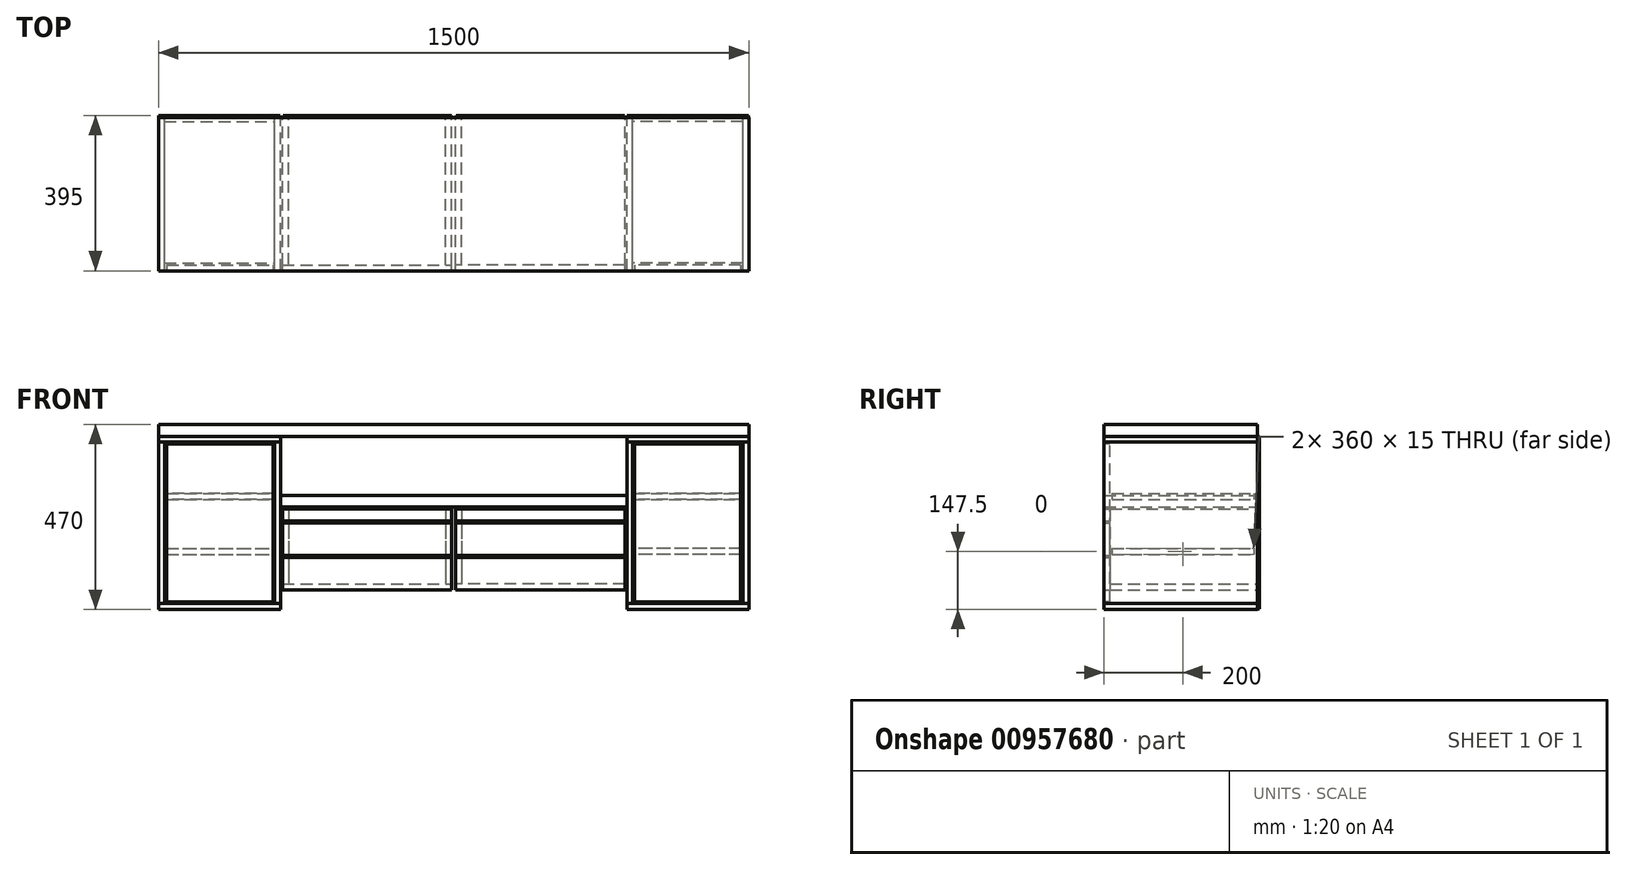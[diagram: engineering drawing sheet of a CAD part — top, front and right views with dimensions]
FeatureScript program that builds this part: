
annotation { "Feature Type Name" : "Feature", "Feature Type Description" : "" }
export const myFeature = defineFeature(function(context is Context, id is Id, definition is map)
    precondition{}
    {
        {
            var Q0;
            Q0=qCreatedBy(makeId("Top.planeOp"),FACE);
            var sketch = newSketch(context, id + "F0", { "sketchPlane" : qUnion([Q0])});
            skLineSegment(sketch, "E0.bottom", {"start": v(0, 0) * mm, "end": v(310, 0) * mm});
            skLineSegment(sketch, "E0.top", {"start": v(0, 390) * mm, "end": v(310, 390) * mm});
            skLineSegment(sketch, "E0.left", {"start": v(0, 0) * mm, "end": v(0, 390) * mm});
            skLineSegment(sketch, "E0.right", {"start": v(310, 0) * mm, "end": v(310, 390) * mm});
            skSolve(sketch);
        }
        {
            var Q0;
            Q0 = qSketchRegion(id + "F0", true);
            extrude(context, id + "F1", {"entities" : qUnion([Q0]), "depth" : 15 * mm, "offsetDistance" : 25 * mm});
        }
        {
            var Q0;
            Q0=makeQuery(id+"F1.opExtrude","CAP_FACE",FACE,{"disambiguationData":[OSD([sQuery(id+"F0.wireOp",EDGE,"E0.bottom"),sQuery(id+"F0.wireOp",EDGE,"E0.top"),sQuery(id+"F0.wireOp",EDGE,"E0.left"),sQuery(id+"F0.wireOp",EDGE,"E0.right")])],"isStart":false});
            cPlane(context, id + "F2", {"entities" : qUnion([Q0]), "cplaneType" : CPlaneType.OFFSET, "offset" : 0 * mm, "width" : 150 * mm, "height" : 150 * mm});
        }
        {
            var Q0;
            Q0=qCreatedBy(id+"F2.planeOp",FACE);
            var sketch = newSketch(context, id + "F3", { "sketchPlane" : qUnion([Q0])});
            skLineSegment(sketch, "E1.bottom", {"start": v(0, 0) * mm, "end": v(15, 0) * mm});
            skLineSegment(sketch, "E1.top", {"start": v(0, 390) * mm, "end": v(15, 390) * mm});
            skLineSegment(sketch, "E1.left", {"start": v(0, 0) * mm, "end": v(0, 390) * mm});
            skLineSegment(sketch, "E1.right", {"start": v(15, 0) * mm, "end": v(15, 390) * mm});
            skLineSegment(sketch, "E2.bottom", {"start": v(310, 0) * mm, "end": v(295, 0) * mm});
            skLineSegment(sketch, "E2.top", {"start": v(310, 390) * mm, "end": v(295, 390) * mm});
            skLineSegment(sketch, "E2.left", {"start": v(310, 0) * mm, "end": v(310, 390) * mm});
            skLineSegment(sketch, "E2.right", {"start": v(295, 0) * mm, "end": v(295, 390) * mm});
            skSolve(sketch);
        }
        {
            var Q0;
            Q0 = qSketchRegion(id + "F3", true);
            extrude(context, id + "F4", {"entities" : qUnion([Q0]), "depth" : 410 * mm, "offsetDistance" : 25 * mm});
        }
        {
            var Q0;
            Q0=makeQuery(id+"F4.opExtrude","CAP_FACE",FACE,{"disambiguationData":[OSD([sQuery(id+"F3.wireOp",EDGE,"E1.bottom"),sQuery(id+"F3.wireOp",EDGE,"E1.top"),sQuery(id+"F3.wireOp",EDGE,"E1.left"),sQuery(id+"F3.wireOp",EDGE,"E1.right")])],"isStart":false});
            var sketch = newSketch(context, id + "F5", { "sketchPlane" : qUnion([Q0])});
            skLineSegment(sketch, "E3.bottom", {"start": v(0, 0) * mm, "end": v(310, 0) * mm});
            skLineSegment(sketch, "E3.top", {"start": v(0, 390) * mm, "end": v(310, 390) * mm});
            skLineSegment(sketch, "E3.left", {"start": v(0, 0) * mm, "end": v(0, 390) * mm});
            skLineSegment(sketch, "E3.right", {"start": v(310, 0) * mm, "end": v(310, 390) * mm});
            skSolve(sketch);
        }
        {
            var Q0;
            Q0 = qSketchRegion(id + "F5", true);
            extrude(context, id + "F6", {"entities" : qUnion([Q0]), "depth" : 15 * mm, "offsetDistance" : 25 * mm});
        }
        {
            var Q0;
            Q0=makeQuery(id+"F6.opExtrude","SWEPT_FACE",FACE,{"disambiguationData":[OSD([sQuery(id+"F5.wireOp",EDGE,"E3.top")])]});
            var sketch = newSketch(context, id + "F7", { "sketchPlane" : qUnion([Q0])});
            skLineSegment(sketch, "E4.bottom", {"start": v(-1, 1) * mm, "end": v(-309, 1) * mm});
            skLineSegment(sketch, "E4.top", {"start": v(-1, 439) * mm, "end": v(-309, 439) * mm});
            skLineSegment(sketch, "E4.left", {"start": v(-1, 1) * mm, "end": v(-1, 439) * mm});
            skLineSegment(sketch, "E4.right", {"start": v(-309, 1) * mm, "end": v(-309, 439) * mm});
            skPoint(sketch, "E5", {"position": v(-310, 432.5) * mm});
            skSolve(sketch);
        }
        {
            var Q0;
            Q0 = qSketchRegion(id + "F7", true);
            extrude(context, id + "F8", {"entities" : qUnion([Q0]), "depth" : 5 * mm, "offsetDistance" : 25 * mm});
        }
        {
            var Q0;
            Q0=makeQuery(id+"F1.opExtrude","CAP_FACE",FACE,{"disambiguationData":[OSD([sQuery(id+"F0.wireOp",EDGE,"E0.bottom"),sQuery(id+"F0.wireOp",EDGE,"E0.top"),sQuery(id+"F0.wireOp",EDGE,"E0.left"),sQuery(id+"F0.wireOp",EDGE,"E0.right")])],"isStart":false});
            cPlane(context, id + "F9", {"entities" : qUnion([Q0]), "cplaneType" : CPlaneType.OFFSET, "offset" : 125 * mm, "width" : 150 * mm, "height" : 150 * mm});
        }
        {
            var Q0;
            Q0=makeQuery(id+"F1.opExtrude","CAP_FACE",FACE,{"disambiguationData":[OSD([sQuery(id+"F0.wireOp",EDGE,"E0.bottom"),sQuery(id+"F0.wireOp",EDGE,"E0.top"),sQuery(id+"F0.wireOp",EDGE,"E0.left"),sQuery(id+"F0.wireOp",EDGE,"E0.right")])],"isStart":false});
            cPlane(context, id + "F10", {"entities" : qUnion([Q0]), "cplaneType" : CPlaneType.OFFSET, "offset" : (125 + 125 + 15) * mm, "width" : 150 * mm, "height" : 150 * mm});
        }
        {
            var Q0;
            Q0=qCreatedBy(id+"F9.planeOp",FACE);
            var sketch = newSketch(context, id + "F11", { "sketchPlane" : qUnion([Q0])});
            skLineSegment(sketch, "E6.bottom", {"start": v(15, 20) * mm, "end": v(295, 20) * mm});
            skLineSegment(sketch, "E6.top", {"start": v(15, 380) * mm, "end": v(295, 380) * mm});
            skLineSegment(sketch, "E6.left", {"start": v(15, 20) * mm, "end": v(15, 380) * mm});
            skLineSegment(sketch, "E6.right", {"start": v(295, 20) * mm, "end": v(295, 380) * mm});
            skSolve(sketch);
        }
        {
            var Q0;
            Q0 = qSketchRegion(id + "F11", true);
            extrude(context, id + "F12", {"entities" : qUnion([Q0]), "operationType" : NewBodyOperationType.ADD, "depth" : 15 * mm, "offsetDistance" : 25 * mm});
        }
        {
            var Q0;
            Q0=qCreatedBy(id+"F10.planeOp",FACE);
            var sketch = newSketch(context, id + "F13", { "sketchPlane" : qUnion([Q0])});
            skLineSegment(sketch, "E7.0.0", {"start": v(295, 380) * mm, "end": v(15, 380) * mm});
            skLineSegment(sketch, "E7.0.1", {"start": v(15, 380) * mm, "end": v(15, 20) * mm});
            skLineSegment(sketch, "E7.0.2", {"start": v(15, 20) * mm, "end": v(295, 20) * mm});
            skLineSegment(sketch, "E7.0.3", {"start": v(295, 20) * mm, "end": v(295, 380) * mm});
            skSolve(sketch);
        }
        {
            var Q0;
            Q0 = qSketchRegion(id + "F13", true);
            extrude(context, id + "F14", {"entities" : qUnion([Q0]), "depth" : 15 * mm, "offsetDistance" : 25 * mm});
        }
        {
            var Q0;
            Q0=makeQuery(id+"F4.opExtrude","SWEPT_FACE",FACE,{"disambiguationData":[OSD([sQuery(id+"F3.wireOp",EDGE,"E2.bottom")])]});
            var sketch = newSketch(context, id + "F15", { "sketchPlane" : qUnion([Q0])});
            skLineSegment(sketch, "E8.bottom", {"start": v(21, 19) * mm, "end": v(291, 19) * mm});
            skLineSegment(sketch, "E8.top", {"start": v(21, 421) * mm, "end": v(291, 421) * mm});
            skLineSegment(sketch, "E8.left", {"start": v(21, 19) * mm, "end": v(21, 421) * mm});
            skLineSegment(sketch, "E8.right", {"start": v(291, 19) * mm, "end": v(291, 421) * mm});
            skSolve(sketch);
        }
        {
            var Q0;
            Q0 = qSketchRegion(id + "F15", true);
            extrude(context, id + "F16", {"entities" : qUnion([Q0]), "oppositeDirection" : true, "depth" : 15 * mm, "offsetDistance" : 25 * mm});
        }
        {
            var Q0;
            Q0=qCreatedBy(makeId("Right.planeOp"),FACE);
            cPlane(context, id + "F17", {"entities" : qUnion([Q0]), "cplaneType" : CPlaneType.OFFSET, "offset" : 750 * mm, "width" : 150 * mm, "height" : 150 * mm});
        }
        {
            var Q0;
            Q0=makeQuery(id+"F1.opExtrude","SWEPT_BODY",BODY,{"disambiguationData":[OSD([sQuery(id+"F0.wireOp",EDGE,"E0.bottom"),sQuery(id+"F0.wireOp",EDGE,"E0.top"),sQuery(id+"F0.wireOp",EDGE,"E0.left"),sQuery(id+"F0.wireOp",EDGE,"E0.right")])]});
            var Q1;
            Q1=makeQuery(id+"F4.opExtrude","SWEPT_BODY",BODY,{"disambiguationData":[OSD([sQuery(id+"F3.wireOp",EDGE,"E1.bottom"),sQuery(id+"F3.wireOp",EDGE,"E1.top"),sQuery(id+"F3.wireOp",EDGE,"E1.left"),sQuery(id+"F3.wireOp",EDGE,"E1.right")])]});
            var Q2;
            Q2=makeQuery(id+"F4.opExtrude","SWEPT_BODY",BODY,{"disambiguationData":[OSD([sQuery(id+"F3.wireOp",EDGE,"E2.bottom"),sQuery(id+"F3.wireOp",EDGE,"E2.top"),sQuery(id+"F3.wireOp",EDGE,"E2.left"),sQuery(id+"F3.wireOp",EDGE,"E2.right")])]});
            var Q3;
            Q3=makeQuery(id+"F8.opExtrude","SWEPT_BODY",BODY,{"disambiguationData":[OSD([sQuery(id+"F7.wireOp",EDGE,"E4.bottom"),sQuery(id+"F7.wireOp",EDGE,"E4.top"),sQuery(id+"F7.wireOp",EDGE,"E4.left"),sQuery(id+"F7.wireOp",EDGE,"E4.right")])]});
            var Q4;
            Q4=makeQuery(id+"F6.opExtrude","SWEPT_BODY",BODY,{"disambiguationData":[OSD([sQuery(id+"F5.wireOp",EDGE,"E3.bottom"),sQuery(id+"F5.wireOp",EDGE,"E3.top"),sQuery(id+"F5.wireOp",EDGE,"E3.left"),sQuery(id+"F5.wireOp",EDGE,"E3.right")])]});
            var Q5;
            Q5=makeQuery(id+"F14.opExtrude","SWEPT_BODY",BODY,{"disambiguationData":[OSD([sQuery(id+"F13.wireOp",EDGE,"E7.0.0"),sQuery(id+"F13.wireOp",EDGE,"E7.0.1"),sQuery(id+"F13.wireOp",EDGE,"E7.0.2"),sQuery(id+"F13.wireOp",EDGE,"E7.0.3")])]});
            var Q6;
            Q6=makeQuery(id+"F16.opExtrude","SWEPT_BODY",BODY,{"disambiguationData":[OSD([sQuery(id+"F15.wireOp",EDGE,"E8.bottom"),sQuery(id+"F15.wireOp",EDGE,"E8.top"),sQuery(id+"F15.wireOp",EDGE,"E8.left"),sQuery(id+"F15.wireOp",EDGE,"E8.right")])]});
            var Q7;
            Q7=qCreatedBy(id+"F17.planeOp",FACE);
            mirror(context, id + "F18", {"entities" : qUnion([Q0, Q1, Q2, Q3, Q4, Q5, Q6]), "mirrorPlane" : qUnion([Q7])});
        }
        {
            var Q0;
            Q0=makeQuery(id+"F6.opExtrude","CAP_FACE",FACE,{"disambiguationData":[OSD([sQuery(id+"F5.wireOp",EDGE,"E3.bottom"),sQuery(id+"F5.wireOp",EDGE,"E3.top"),sQuery(id+"F5.wireOp",EDGE,"E3.left"),sQuery(id+"F5.wireOp",EDGE,"E3.right")])],"isStart":false});
            var sketch = newSketch(context, id + "F19", { "sketchPlane" : qUnion([Q0])});
            skLineSegment(sketch, "E9.bottom", {"start": v(0, 0) * mm, "end": v(1500, 0) * mm});
            skLineSegment(sketch, "E9.top", {"start": v(0, 390) * mm, "end": v(1500, 390) * mm});
            skLineSegment(sketch, "E9.left", {"start": v(0, 0) * mm, "end": v(0, 390) * mm});
            skLineSegment(sketch, "E9.right", {"start": v(1500, 0) * mm, "end": v(1500, 390) * mm});
            skSolve(sketch);
        }
        {
            var Q0;
            Q0 = qSketchRegion(id + "F19", true);
            extrude(context, id + "F20", {"entities" : qUnion([Q0]), "depth" : 30 * mm, "offsetDistance" : 25 * mm});
        }
        {
            var Q0;
            Q0=makeQuery(id+"F20.opExtrude","CAP_FACE",FACE,{"disambiguationData":[OSD([sQuery(id+"F19.wireOp",EDGE,"E9.bottom"),sQuery(id+"F19.wireOp",EDGE,"E9.top"),sQuery(id+"F19.wireOp",EDGE,"E9.left"),sQuery(id+"F19.wireOp",EDGE,"E9.right")])],"isStart":true});
            cPlane(context, id + "F21", {"entities" : qUnion([Q0]), "cplaneType" : CPlaneType.OFFSET, "offset" : 180 * mm, "width" : 150 * mm, "height" : 150 * mm});
        }
        {
            var Q0;
            Q0=qCreatedBy(id+"F21.planeOp",FACE);
            var sketch = newSketch(context, id + "F22", { "sketchPlane" : qUnion([Q0])});
            skLineSegment(sketch, "E10.bottom", {"start": v(310, 0) * mm, "end": v(1190, 0) * mm});
            skLineSegment(sketch, "E10.top", {"start": v(310, -390) * mm, "end": v(1190, -390) * mm});
            skLineSegment(sketch, "E10.left", {"start": v(310, 0) * mm, "end": v(310, -390) * mm});
            skLineSegment(sketch, "E10.right", {"start": v(1190, 0) * mm, "end": v(1190, -390) * mm});
            skSolve(sketch);
        }
        {
            var Q0;
            Q0 = qSketchRegion(id + "F22", true);
            extrude(context, id + "F23", {"entities" : qUnion([Q0]), "oppositeDirection" : true, "depth" : 30 * mm, "offsetDistance" : 25 * mm});
        }
        {
            var Q0;
            Q0=qCreatedBy(makeId("Top.planeOp"),FACE);
            cPlane(context, id + "F24", {"entities" : qUnion([Q0]), "cplaneType" : CPlaneType.OFFSET, "offset" : 50 * mm, "width" : 150 * mm, "height" : 150 * mm});
        }
        {
            var Q0;
            Q0=qCreatedBy(id+"F24.planeOp",FACE);
            var sketch = newSketch(context, id + "F25", { "sketchPlane" : qUnion([Q0])});
            skLineSegment(sketch, "E11.bottom", {"start": v(315, 15) * mm, "end": v(745, 15) * mm});
            skLineSegment(sketch, "E11.top", {"start": v(315, 390) * mm, "end": v(745, 390) * mm});
            skLineSegment(sketch, "E11.left", {"start": v(315, 15) * mm, "end": v(315, 390) * mm});
            skLineSegment(sketch, "E11.right", {"start": v(745, 15) * mm, "end": v(745, 390) * mm});
            skSolve(sketch);
        }
        {
            var Q0;
            Q0 = qSketchRegion(id + "F25", true);
            extrude(context, id + "F26", {"entities" : qUnion([Q0]), "depth" : 15 * mm, "offsetDistance" : 25 * mm});
        }
        {
            var Q0;
            Q0=makeQuery(id+"F26.opExtrude","CAP_FACE",FACE,{"disambiguationData":[OSD([sQuery(id+"F25.wireOp",EDGE,"E11.bottom"),sQuery(id+"F25.wireOp",EDGE,"E11.top"),sQuery(id+"F25.wireOp",EDGE,"E11.left"),sQuery(id+"F25.wireOp",EDGE,"E11.right")])],"isStart":false});
            var sketch = newSketch(context, id + "F27", { "sketchPlane" : qUnion([Q0])});
            skLineSegment(sketch, "E12.bottom", {"start": v(315, 15) * mm, "end": v(330, 15) * mm});
            skLineSegment(sketch, "E12.top", {"start": v(315, 390) * mm, "end": v(330, 390) * mm});
            skLineSegment(sketch, "E12.left", {"start": v(315, 15) * mm, "end": v(315, 390) * mm});
            skLineSegment(sketch, "E12.right", {"start": v(330, 15) * mm, "end": v(330, 390) * mm});
            skLineSegment(sketch, "E13.bottom", {"start": v(745, 15) * mm, "end": v(730, 15) * mm});
            skLineSegment(sketch, "E13.top", {"start": v(745, 390) * mm, "end": v(730, 390) * mm});
            skLineSegment(sketch, "E13.left", {"start": v(745, 15) * mm, "end": v(745, 390) * mm});
            skLineSegment(sketch, "E13.right", {"start": v(730, 15) * mm, "end": v(730, 390) * mm});
            skSolve(sketch);
        }
        {
            var Q0;
            Q0 = qSketchRegion(id + "F27", true);
            extrude(context, id + "F28", {"entities" : qUnion([Q0]), "depth" : 190 * mm, "offsetDistance" : 25 * mm});
        }
        {
            var Q0;
            Q0=makeQuery(id+"F28.boolean.opBoolean","MERGE",FACE,{"derivedFrom":[makeQuery(id+"F26.opExtrude","SWEPT_FACE",FACE,{"disambiguationData":[OSD([sQuery(id+"F25.wireOp",EDGE,"E11.bottom")])]}),makeQuery(id+"F28.opExtrude","SWEPT_FACE",FACE,{"disambiguationData":[OSD([sQuery(id+"F27.wireOp",EDGE,"E12.bottom")])]}),makeQuery(id+"F28.opExtrude","SWEPT_FACE",FACE,{"disambiguationData":[OSD([sQuery(id+"F27.wireOp",EDGE,"E13.bottom")])]})]});
            var sketch = newSketch(context, id + "F29", { "sketchPlane" : qUnion([Q0])});
            skLineSegment(sketch, "E14.bottom", {"start": v(315, 50) * mm, "end": v(745, 50) * mm});
            skLineSegment(sketch, "E14.top", {"start": v(315, 132.5) * mm, "end": v(745, 132.5) * mm});
            skLineSegment(sketch, "E14.left", {"start": v(315, 50) * mm, "end": v(315, 132.5) * mm});
            skLineSegment(sketch, "E14.right", {"start": v(745, 50) * mm, "end": v(745, 132.5) * mm});
            skLineSegment(sketch, "E15.bottom", {"start": v(315, 137.5) * mm, "end": v(745, 137.5) * mm});
            skLineSegment(sketch, "E15.top", {"start": v(315, 220) * mm, "end": v(745, 220) * mm});
            skLineSegment(sketch, "E15.left", {"start": v(315, 137.5) * mm, "end": v(315, 220) * mm});
            skLineSegment(sketch, "E15.right", {"start": v(745, 137.5) * mm, "end": v(745, 220) * mm});
            skLineSegment(sketch, "E16.bottom", {"start": v(315, 255) * mm, "end": v(745, 255) * mm});
            skLineSegment(sketch, "E16.top", {"start": v(315, 225) * mm, "end": v(745, 225) * mm});
            skLineSegment(sketch, "E16.left", {"start": v(315, 255) * mm, "end": v(315, 225) * mm});
            skLineSegment(sketch, "E16.right", {"start": v(745, 255) * mm, "end": v(745, 225) * mm});
            skSolve(sketch);
        }
        {
            var Q0;
            Q0 = qSketchRegion(id + "F29", true);
            extrude(context, id + "F30", {"entities" : qUnion([Q0]), "depth" : 15 * mm, "offsetDistance" : 25 * mm});
        }
        {
            var Q0;
            Q0=makeQuery(id+"F28.boolean.opBoolean","MERGE",FACE,{"derivedFrom":[makeQuery(id+"F26.opExtrude","SWEPT_FACE",FACE,{"disambiguationData":[OSD([sQuery(id+"F25.wireOp",EDGE,"E11.top")])]}),makeQuery(id+"F28.opExtrude","SWEPT_FACE",FACE,{"disambiguationData":[OSD([sQuery(id+"F27.wireOp",EDGE,"E12.top")])]}),makeQuery(id+"F28.opExtrude","SWEPT_FACE",FACE,{"disambiguationData":[OSD([sQuery(id+"F27.wireOp",EDGE,"E13.top")])]})]});
            var sketch = newSketch(context, id + "F31", { "sketchPlane" : qUnion([Q0])});
            skLineSegment(sketch, "E17.bottom", {"start": v(-744, 254) * mm, "end": v(-316, 254) * mm});
            skLineSegment(sketch, "E17.top", {"start": v(-744, 51) * mm, "end": v(-316, 51) * mm});
            skLineSegment(sketch, "E17.left", {"start": v(-744, 254) * mm, "end": v(-744, 51) * mm});
            skLineSegment(sketch, "E17.right", {"start": v(-316, 254) * mm, "end": v(-316, 51) * mm});
            skSolve(sketch);
        }
        {
            var Q0;
            Q0 = qSketchRegion(id + "F31", true);
            extrude(context, id + "F32", {"entities" : qUnion([Q0]), "depth" : 5 * mm, "offsetDistance" : 25 * mm});
        }
        {
            var Q0;
            Q0=makeQuery(id+"F26.opExtrude","SWEPT_BODY",BODY,{"disambiguationData":[OSD([sQuery(id+"F25.wireOp",EDGE,"E11.bottom"),sQuery(id+"F25.wireOp",EDGE,"E11.top"),sQuery(id+"F25.wireOp",EDGE,"E11.left"),sQuery(id+"F25.wireOp",EDGE,"E11.right")])]});
            var Q1;
            Q1=makeQuery(id+"F30.opExtrude","SWEPT_BODY",BODY,{"disambiguationData":[OSD([sQuery(id+"F29.wireOp",EDGE,"E16.bottom"),sQuery(id+"F29.wireOp",EDGE,"E16.top"),sQuery(id+"F29.wireOp",EDGE,"E16.left"),sQuery(id+"F29.wireOp",EDGE,"E16.right")])]});
            var Q2;
            Q2=makeQuery(id+"F30.opExtrude","SWEPT_BODY",BODY,{"disambiguationData":[OSD([sQuery(id+"F29.wireOp",EDGE,"E15.bottom"),sQuery(id+"F29.wireOp",EDGE,"E15.top"),sQuery(id+"F29.wireOp",EDGE,"E15.left"),sQuery(id+"F29.wireOp",EDGE,"E15.right")])]});
            var Q3;
            Q3=makeQuery(id+"F30.opExtrude","SWEPT_BODY",BODY,{"disambiguationData":[OSD([sQuery(id+"F29.wireOp",EDGE,"E14.bottom"),sQuery(id+"F29.wireOp",EDGE,"E14.top"),sQuery(id+"F29.wireOp",EDGE,"E14.left"),sQuery(id+"F29.wireOp",EDGE,"E14.right")])]});
            var Q4;
            Q4=makeQuery(id+"F28.opExtrude","SWEPT_BODY",BODY,{"disambiguationData":[OSD([sQuery(id+"F27.wireOp",EDGE,"E13.bottom"),sQuery(id+"F27.wireOp",EDGE,"E13.top"),sQuery(id+"F27.wireOp",EDGE,"E13.left"),sQuery(id+"F27.wireOp",EDGE,"E13.right")])]});
            var Q5;
            Q5=makeQuery(id+"F32.opExtrude","SWEPT_BODY",BODY,{"disambiguationData":[OSD([sQuery(id+"F31.wireOp",EDGE,"E17.bottom"),sQuery(id+"F31.wireOp",EDGE,"E17.top"),sQuery(id+"F31.wireOp",EDGE,"E17.left"),sQuery(id+"F31.wireOp",EDGE,"E17.right")])]});
            var Q6;
            Q6=qCreatedBy(id+"F17.planeOp",FACE);
            mirror(context, id + "F33", {"entities" : qUnion([Q0, Q1, Q2, Q3, Q4, Q5]), "mirrorPlane" : qUnion([Q6])});
        }
    });
